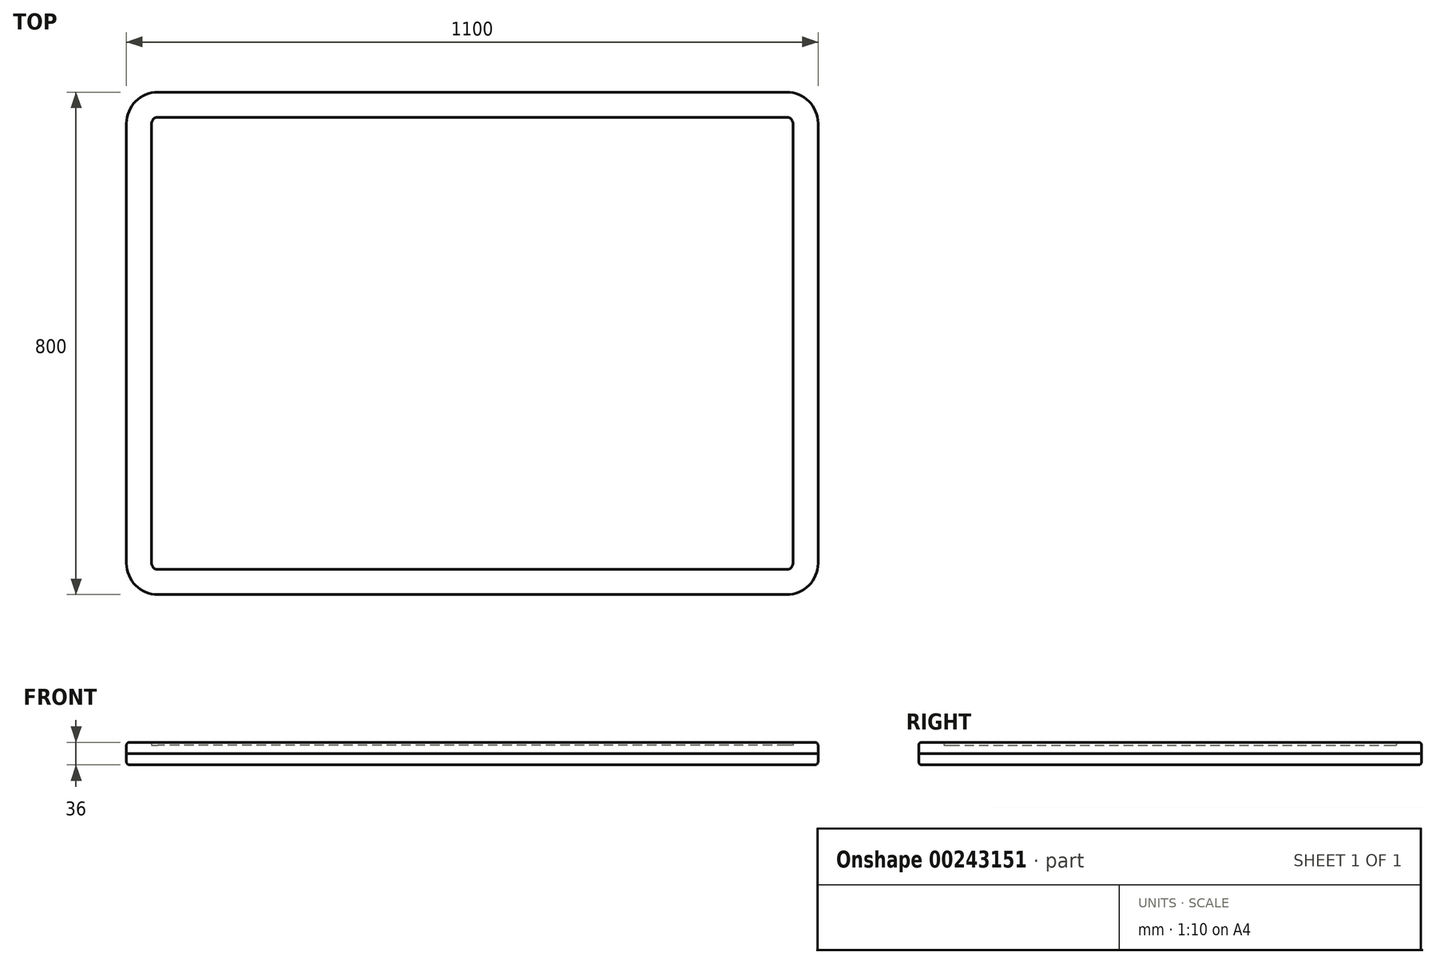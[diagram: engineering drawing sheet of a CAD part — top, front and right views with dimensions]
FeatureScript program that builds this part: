
annotation { "Feature Type Name" : "Feature", "Feature Type Description" : "" }
export const myFeature = defineFeature(function(context is Context, id is Id, definition is map)
    precondition{}
    {
        {
            var Q0;
            Q0=qCreatedBy(makeId("Top.planeOp"),FACE);
            var sketch = newSketch(context, id + "F0", { "sketchPlane" : qUnion([Q0])});
            skLineSegment(sketch, "E0.bottom", {"start": v(-500, 400) * mm, "end": v(500, 400) * mm});
            skLineSegment(sketch, "E0.top", {"start": v(-500, -400) * mm, "end": v(500, -400) * mm});
            skLineSegment(sketch, "E0.left", {"start": v(-550, 350) * mm, "end": v(-550, -350) * mm});
            skLineSegment(sketch, "E0.right", {"start": v(550, 350) * mm, "end": v(550, -350) * mm});
            skPoint(sketch, "E0.middle", {"position": v(0, 0) * mm});
            skPoint(sketch, "E1.visualSharp", {"position": v(-550, 400) * mm});
            skArc(sketch, "E1.filletArc", {"start": v(-500, 400) * mm, "mid": v(-535.36, 385.36) * mm, "end": v(-550, 350) * mm});
            skPoint(sketch, "E2.visualSharp", {"position": v(550, 400) * mm});
            skArc(sketch, "E2.filletArc", {"start": v(550, 350) * mm, "mid": v(535.36, 385.36) * mm, "end": v(500, 400) * mm});
            skPoint(sketch, "E3.visualSharp", {"position": v(550, -400) * mm});
            skArc(sketch, "E3.filletArc", {"start": v(500, -400) * mm, "mid": v(535.36, -385.36) * mm, "end": v(550, -350) * mm});
            skPoint(sketch, "E4.visualSharp", {"position": v(-550, -400) * mm});
            skArc(sketch, "E4.filletArc", {"start": v(-550, -350) * mm, "mid": v(-535.36, -385.36) * mm, "end": v(-500, -400) * mm});
            skLineSegment(sketch, "E5.bottom", {"start": v(-500, 360) * mm, "end": v(500, 360) * mm});
            skLineSegment(sketch, "E5.top", {"start": v(-500, -360) * mm, "end": v(500, -360) * mm});
            skLineSegment(sketch, "E5.left", {"start": v(-510, 350) * mm, "end": v(-510, -350) * mm});
            skLineSegment(sketch, "E5.right", {"start": v(510, 350) * mm, "end": v(510, -350) * mm});
            skPoint(sketch, "E6.visualSharp", {"position": v(-510, 360) * mm});
            skArc(sketch, "E6.filletArc", {"start": v(-500, 360) * mm, "mid": v(-507.07, 357.07) * mm, "end": v(-510, 350) * mm});
            skPoint(sketch, "E7.visualSharp", {"position": v(510, 360) * mm});
            skArc(sketch, "E7.filletArc", {"start": v(510, 350) * mm, "mid": v(507.07, 357.07) * mm, "end": v(500, 360) * mm});
            skPoint(sketch, "E8.visualSharp", {"position": v(510, -360) * mm});
            skArc(sketch, "E8.filletArc", {"start": v(500, -360) * mm, "mid": v(507.07, -357.07) * mm, "end": v(510, -350) * mm});
            skPoint(sketch, "E9.visualSharp", {"position": v(-510, -360) * mm});
            skArc(sketch, "E9.filletArc", {"start": v(-510, -350) * mm, "mid": v(-507.07, -357.07) * mm, "end": v(-500, -360) * mm});
            skSolve(sketch);
        }
        {
            var Q0;
            Q0 = qSketchRegion(id + "F0", true);
            var Q1;
            Q1=makeQuery(id+"F0.imprint","IMPRINT",FACE,{"disambiguationData":[TD([[makeQuery(id+"F0.imprint","IMPRINT",EDGE,{"derivedFrom":sQuery(id+"F0.wireOp",EDGE,"E5.bottom")}),-1.0]])]});
            extrude(context, id + "F1", {"entities" : qUnion([Q0, Q1]), "depth" : 13 * mm});
        }
        {
            var Q0;
            Q0=makeQuery(id+"F0.imprint","IMPRINT",FACE,{"disambiguationData":[TD([[makeQuery(id+"F0.imprint","IMPRINT",EDGE,{"derivedFrom":sQuery(id+"F0.wireOp",EDGE,"E0.bottom")}),-1.0]])]});
            extrude(context, id + "F2", {"entities" : qUnion([Q0]), "operationType" : NewBodyOperationType.ADD, "depth" : 18 * mm});
        }
        {
            var Q0;
            Q0=makeQuery(id+"F0.imprint","IMPRINT",FACE,{"disambiguationData":[TD([[makeQuery(id+"F0.imprint","IMPRINT",EDGE,{"derivedFrom":sQuery(id+"F0.wireOp",EDGE,"E0.bottom")}),-1.0]])]});
            var Q1;
            Q1=makeQuery(id+"F0.imprint","IMPRINT",FACE,{"disambiguationData":[TD([[makeQuery(id+"F0.imprint","IMPRINT",EDGE,{"derivedFrom":sQuery(id+"F0.wireOp",EDGE,"E5.bottom")}),-1.0]])]});
            extrude(context, id + "F3", {"entities" : qUnion([Q0, Q1]), "oppositeDirection" : true, "depth" : 18 * mm});
        }
        {
            var Q0;
            Q0=makeQuery(id+"F2.opExtrude","CAP_EDGE",EDGE,{"disambiguationData":[OSD([sQuery(id+"F0.wireOp",EDGE,"E0.right")])],"isStart":false});
            fillet(context, id + "F4", {"entities" : qUnion([Q0]), "radius" : 5 * mm, "tangentPropagation" : true, "allowEdgeOverflow" : false});
        }
        {
            var Q0;
            Q0=makeQuery(id+"F3.opExtrude","CAP_EDGE",EDGE,{"disambiguationData":[OSD([sQuery(id+"F0.wireOp",EDGE,"E0.right")])],"isStart":false});
            fillet(context, id + "F5", {"entities" : qUnion([Q0]), "radius" : 5 * mm, "tangentPropagation" : true, "allowEdgeOverflow" : false});
        }
    });
